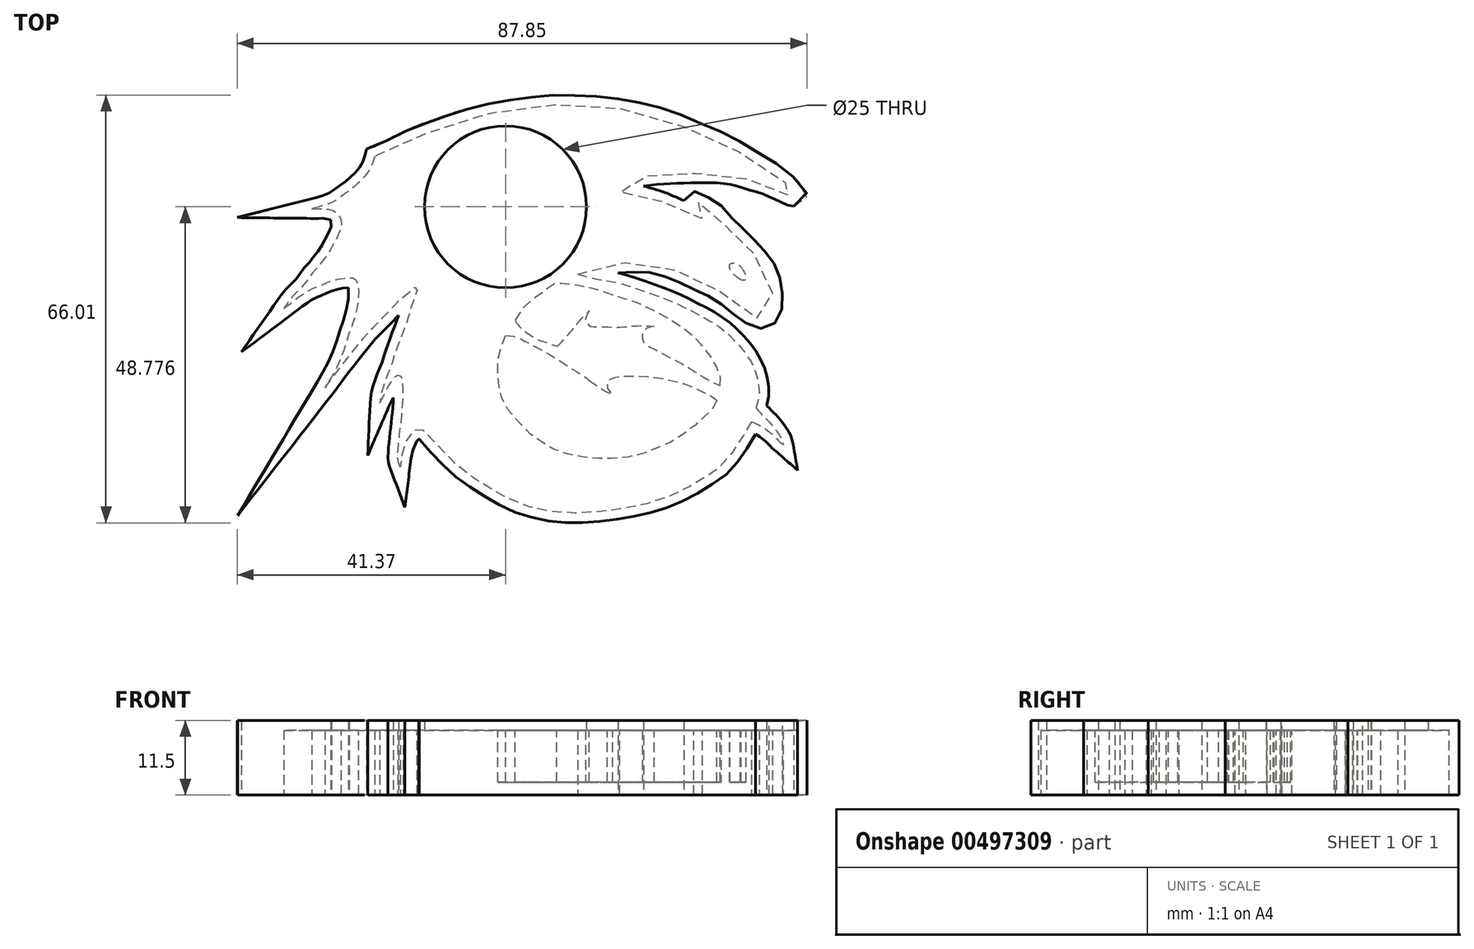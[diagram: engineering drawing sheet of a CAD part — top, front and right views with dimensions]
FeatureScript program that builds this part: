
annotation { "Feature Type Name" : "Feature", "Feature Type Description" : "" }
export const myFeature = defineFeature(function(context is Context, id is Id, definition is map)
    precondition{}
    {
        {
            var Q0;
            Q0=qCreatedBy(makeId("Top.planeOp"),FACE);
            var sketch = newSketch(context, id + "F0", { "sketchPlane" : qUnion([Q0])});
            skFitSpline(sketch, "E0", {"points": [v(3.09, 6.25) * mm, v(4.8, 5.75) * mm, v(7.76, 5.16) * mm, v(10.6, 4.54) * mm, v(13.82, 3.41) * mm, v(16.32, 2.53) * mm, v(19.29, 1.24) * mm, v(22.8, -0.6) * mm, v(25.68, -2.48) * mm, v(28.6, -5.48) * mm, v(30.18, -7.98) * mm, v(31.06, -11) * mm, v(30.99, -13.07) * mm, v(30.6, -14.4) * mm], "startDerivative": vector(25.97, -8.42) * mm, "endDerivative": vector(-8.12, -23.78) * mm});
            skFitSpline(sketch, "E1", {"points": [v(30.6, -14.4) * mm, v(31.45, -15.39) * mm, v(32.64, -16.58) * mm, v(33.62, -17.77) * mm, v(34.57, -19.25) * mm, v(34.82, -20.13) * mm], "startDerivative": vector(4.09, -5.06) * mm, "endDerivative": vector(0.92, -5.16) * mm});
            skFitSpline(sketch, "E2", {"points": [v(29.94, -16.55) * mm, v(30.85, -16.97) * mm, v(31.87, -17.53) * mm, v(32.92, -18.34) * mm, v(33.48, -18.86) * mm, v(34.12, -19.5) * mm, v(34.82, -20.13) * mm], "startDerivative": vector(5.46, -2.46) * mm, "endDerivative": vector(4.4, -3.84) * mm});
            skFitSpline(sketch, "E3", {"points": [v(29.94, -16.55) * mm, v(29.06, -18.02) * mm, v(27.3, -20.83) * mm, v(25.2, -23.43) * mm, v(23.33, -24.76) * mm, v(21.5, -25.92) * mm, v(18.98, -27.3) * mm, v(15.08, -28.84) * mm, v(11.5, -29.71) * mm, v(7.11, -30.38) * mm, v(2.02, -30.66) * mm, v(-2.2, -30.2) * mm, v(-5.85, -29.19) * mm, v(-9.43, -27.43) * mm, v(-11.67, -26.03) * mm, v(-14.98, -23.78) * mm, v(-16.73, -22.02) * mm, v(-17.85, -20.9) * mm, v(-19.19, -19.42) * mm, v(-20.6, -17.91) * mm, v(-21.12, -17.74) * mm, v(-21.82, -17.74) * mm, v(-22.6, -18.3) * mm, v(-23.26, -19.28) * mm, v(-23.82, -20.9) * mm, v(-24.1, -22.27) * mm, v(-24.28, -23.57) * mm], "startDerivative": vector(-24.88, -41.9) * mm, "endDerivative": vector(-5.74, -46.22) * mm});
            skFitSpline(sketch, "E4", {"points": [v(-24.28, -23.57) * mm, v(-24.6, -22.55) * mm, v(-24.6, -20.86) * mm, v(-24.08, -16.12) * mm, v(-23.88, -13.88) * mm, v(-23.8, -11.03) * mm, v(-23.93, -10) * mm, v(-24.02, -9.67) * mm, v(-24.49, -9.38) * mm, v(-24.95, -9.52) * mm, v(-25.48, -10.11) * mm, v(-26.07, -10.96) * mm, v(-26.6, -12.05) * mm, v(-27.12, -13.03) * mm, v(-27.4, -13.65) * mm], "startDerivative": vector(-5.7, 15.12) * mm, "endDerivative": vector(-4.81, -11.17) * mm});
            skFitSpline(sketch, "E5", {"points": [v(3.09, 6.25) * mm, v(4.64, 6.94) * mm, v(7.65, 7.65) * mm, v(10.1, 7.98) * mm, v(12.79, 8.07) * mm, v(15.27, 7.8) * mm, v(18.1, 6.88) * mm, v(20.5, 5.82) * mm, v(22.6, 4.82) * mm, v(25.07, 3.55) * mm, v(27.43, 1.75) * mm, v(28.64, 0.8) * mm, v(30.36, -0.32) * mm, v(31.42, -0.67) * mm, v(32.34, -0.4) * mm, v(32.9, 0.48) * mm, v(33.22, 1.8) * mm, v(33.1, 3.93) * mm, v(32.69, 5.85) * mm, v(31.83, 7.47) * mm, v(30.36, 9.3) * mm, v(28.97, 10.75) * mm, v(27.29, 12.38) * mm, v(26.34, 13.09) * mm, v(25.6, 14.09) * mm, v(24.6, 15.33) * mm, v(23.68, 16.04) * mm, v(22.5, 16.78) * mm, v(21.76, 17.22) * mm, v(21.23, 17.48) * mm, v(21.03, 17.43) * mm, v(21.08, 17.1) * mm, v(21.59, 16.54) * mm, v(22.18, 15.65) * mm, v(22.33, 14.89) * mm, v(22.06, 14.8) * mm, v(20.88, 15.42) * mm, v(18.75, 16.24) * mm, v(16.83, 17.1) * mm, v(14.74, 17.84) * mm, v(12.52, 18.43) * mm, v(10.43, 18.75) * mm, v(9.66, 18.93) * mm, v(9.66, 19.26) * mm, v(10.22, 20.14) * mm, v(10.72, 20.82) * mm, v(11.9, 21.12) * mm, v(14.94, 21.53) * mm, v(17.78, 21.7) * mm, v(20.08, 21.8) * mm, v(21.91, 21.8) * mm, v(24.8, 21.8) * mm, v(27.55, 21.38) * mm, v(29.68, 20.76) * mm, v(31.95, 20.08) * mm, v(34.7, 18.87) * mm, v(35.35, 18.58) * mm, v(36.09, 18.22) * mm, v(36.5, 18.22) * mm, v(36.85, 18.22) * mm, v(36.91, 18.64) * mm, v(36.09, 19.4) * mm, v(35.26, 20.2) * mm, v(32.6, 22.2) * mm, v(30.2, 23.66) * mm, v(27.2, 25.52) * mm, v(24.54, 26.85) * mm, v(20.64, 28.44) * mm, v(16.95, 30) * mm, v(12.4, 31.19) * mm, v(7.18, 32.07) * mm, v(2.6, 32.28) * mm, v(-1, 32.3) * mm, v(-6.2, 31.72) * mm, v(-10.07, 31.1) * mm, v(-14.88, 29.83) * mm, v(-18.4, 28.62) * mm, v(-22.5, 27.05) * mm, v(-25.6, 25.52) * mm, v(-28.23, 24.4) * mm], "startDerivative": vector(116.8, 60.87) * mm, "endDerivative": vector(-171.2, -68.47) * mm});
            skFitSpline(sketch, "E6", {"points": [v(-28.23, 24.4) * mm, v(-28.63, 23.07) * mm, v(-29.25, 21.96) * mm, v(-30.18, 20.79) * mm, v(-30.96, 20.06) * mm, v(-32.06, 19.15) * mm, v(-33, 18.48) * mm, v(-34.45, 17.49) * mm, v(-35.75, 16.93) * mm, v(-36.77, 16.62) * mm, v(-37.92, 16.32) * mm], "startDerivative": vector(-3.46, -13.35) * mm, "endDerivative": vector(-12.33, -3.13) * mm});
            skFitSpline(sketch, "E7", {"points": [v(-37.92, 16.32) * mm, v(-37.08, 16.32) * mm, v(-35.93, 16.32) * mm, v(-34.87, 16.12) * mm, v(-33.93, 15.61) * mm, v(-33.38, 14.44) * mm, v(-33.4, 13.43) * mm, v(-33.98, 11.97) * mm, v(-34.56, 10.86) * mm, v(-35.42, 9.34) * mm, v(-36.16, 8.35) * mm, v(-36.8, 7.5) * mm, v(-37.74, 6.43) * mm, v(-38.78, 5.04) * mm, v(-39.74, 3.92) * mm, v(-40.87, 2.76) * mm, v(-41.5, 1.97) * mm, v(-42.24, 0.93) * mm], "startDerivative": vector(16.65, -0.2) * mm, "endDerivative": vector(-12.9, -18.49) * mm});
            skFitSpline(sketch, "E8", {"points": [v(-42.24, 0.93) * mm, v(-41.28, 1.65) * mm, v(-40.12, 2.53) * mm, v(-39, 3.32) * mm, v(-38, 3.94) * mm, v(-36.9, 4.36) * mm, v(-35.5, 4.96) * mm, v(-34.64, 5.26) * mm, v(-33.37, 5.54) * mm, v(-32.45, 5.63) * mm, v(-31.68, 5.65) * mm, v(-31.46, 5.58) * mm, v(-31.26, 5.46) * mm, v(-31.11, 5.32) * mm, v(-30.95, 5.06) * mm, v(-30.83, 4.59) * mm, v(-30.67, 3.93) * mm, v(-30.7, 2.67) * mm, v(-30.82, 1.77) * mm, v(-31.02, 0.8) * mm, v(-31.38, -0.8) * mm, v(-31.68, -1.68) * mm, v(-32.18, -2.98) * mm, v(-32.46, -3.97) * mm, v(-32.82, -5.11) * mm, v(-33.37, -6.55) * mm, v(-33.8, -7.58) * mm, v(-34.64, -9.21) * mm, v(-35.87, -11.33) * mm], "startDerivative": vector(24.05, 17.91) * mm, "endDerivative": vector(-22.98, -38.6) * mm});
            skFitSpline(sketch, "E9", {"points": [v(-35.87, -11.33) * mm, v(-34.97, -10.16) * mm, v(-33.96, -8.77) * mm, v(-32.96, -7.45) * mm, v(-32.2, -6.5) * mm, v(-31.24, -5.27) * mm, v(-30.36, -4.17) * mm, v(-28.88, -2.43) * mm, v(-27.5, -1.08) * mm, v(-26.2, 0.3) * mm, v(-24.74, 1.83) * mm, v(-23.95, 2.61) * mm, v(-23.17, 3.17) * mm, v(-22.6, 3.66) * mm, v(-22.16, 4.08) * mm, v(-21.93, 4.25) * mm, v(-21.79, 4.23) * mm, v(-21.68, 4.16) * mm, v(-21.67, 3.75) * mm, v(-21.98, 2.75) * mm, v(-22.32, 1.8) * mm, v(-22.78, 0.46) * mm, v(-23.2, -0.96) * mm, v(-23.52, -1.93) * mm, v(-23.94, -2.95) * mm, v(-24.4, -4.23) * mm, v(-24.87, -5.43) * mm, v(-25.32, -6.7) * mm, v(-25.58, -7.62) * mm, v(-25.96, -8.7) * mm, v(-26.49, -9.94) * mm, v(-26.84, -11) * mm, v(-27.16, -12) * mm, v(-27.35, -12.92) * mm, v(-27.4, -13.65) * mm], "startDerivative": vector(26.23, 33.62) * mm, "endDerivative": vector(-1.36, -29.73) * mm});
            skSolve(sketch);
        }
        {
            var Q0;
            Q0=makeQuery(id+"F0.imprint","IMPRINT",FACE,{"disambiguationData":[TD([[makeQuery(id+"F0.imprint","IMPRINT",EDGE,{"derivedFrom":sQuery(id+"F0.wireOp",EDGE,"E0")}),-1.0]])]});
            extrude(context, id + "F1", {"entities" : qUnion([Q0]), "depth" : 10 * mm});
        }
        {
            var Q0;
            Q0=makeQuery(id+"F1.opExtrude","CAP_FACE",FACE,{"disambiguationData":[OSD([sQuery(id+"F0.wireOp",EDGE,"E0"),sQuery(id+"F0.wireOp",EDGE,"E1"),sQuery(id+"F0.wireOp",EDGE,"E2"),sQuery(id+"F0.wireOp",EDGE,"E3"),sQuery(id+"F0.wireOp",EDGE,"E4"),sQuery(id+"F0.wireOp",EDGE,"E5"),sQuery(id+"F0.wireOp",EDGE,"E6"),sQuery(id+"F0.wireOp",EDGE,"E7"),sQuery(id+"F0.wireOp",EDGE,"E8"),sQuery(id+"F0.wireOp",EDGE,"E9")])],"isStart":true});
            shell(context, id + "F2", {"entities" : qUnion([Q0]), "thickness" : 1.5 * mm, "oppositeDirection" : true});
        }
        {
            var Q0;
            Q0=makeQuery(id+"F2.opShell","OFFSET_FACE",FACE,{"disambiguationData":[OSD([sQuery(id+"F0.wireOp",EDGE,"E0"),sQuery(id+"F0.wireOp",EDGE,"E1"),sQuery(id+"F0.wireOp",EDGE,"E2"),sQuery(id+"F0.wireOp",EDGE,"E3"),sQuery(id+"F0.wireOp",EDGE,"E4"),sQuery(id+"F0.wireOp",EDGE,"E5"),sQuery(id+"F0.wireOp",EDGE,"E6"),sQuery(id+"F0.wireOp",EDGE,"E7"),sQuery(id+"F0.wireOp",EDGE,"E8"),sQuery(id+"F0.wireOp",EDGE,"E9")])]});
            var sketch = newSketch(context, id + "F3", { "sketchPlane" : qUnion([Q0])});
            skFitSpline(sketch, "E10", {"points": [v(-6.56, 0.95) * mm, v(-6.07, 1.61) * mm, v(-5.28, 2.41) * mm, v(-4.25, 3.16) * mm, v(-3.06, 3.86) * mm, v(-1.8, 4.3) * mm, v(-0.16, 4.92) * mm], "startDerivative": vector(3.32, 4.88) * mm, "endDerivative": vector(8.62, 3.44) * mm});
            skFitSpline(sketch, "E11", {"points": [v(-0.16, 4.92) * mm, v(0.34, 4.55) * mm, v(1.64, 3.1) * mm, v(2.57, 2.04) * mm, v(3.18, 1.25) * mm, v(3.86, 0.46) * mm, v(4.9, -0.56) * mm], "startDerivative": vector(3.71, -2.34) * mm, "endDerivative": vector(6, -5.72) * mm});
            skFitSpline(sketch, "E12", {"points": [v(4.9, -0.56) * mm, v(4.4, 0.38) * mm, v(4.33, 1.02) * mm, v(4.66, 1.48) * mm, v(5.15, 1.82) * mm, v(6.26, 1.89) * mm, v(7.63, 1.92) * mm, v(9.23, 1.98) * mm, v(10.99, 1.85) * mm, v(13.05, 1.73) * mm, v(14.9, 1.86) * mm], "startDerivative": vector(-6.25, 10.25) * mm, "endDerivative": vector(14.61, 1.57) * mm});
            skFitSpline(sketch, "E13", {"points": [v(14.9, 1.86) * mm, v(14, 2.05) * mm, v(13.36, 2.44) * mm, v(13.08, 3) * mm, v(13.13, 3.99) * mm, v(13.5, 4.56) * mm, v(14.74, 5.24) * mm, v(15.65, 5.72) * mm, v(16.52, 6.22) * mm, v(18.64, 7.3) * mm, v(20.47, 8.35) * mm, v(21.88, 9.28) * mm, v(22.97, 9.93) * mm, v(24.2, 10.63) * mm, v(25.05, 10.98) * mm], "startDerivative": vector(-14.88, 2.11) * mm, "endDerivative": vector(12.87, 4.55) * mm});
            skFitSpline(sketch, "E14", {"points": [v(25.05, 10.98) * mm, v(25.2, 10.46) * mm, v(24.99, 9.12) * mm, v(24.41, 7.8) * mm, v(23.12, 5.75) * mm, v(21.57, 4.02) * mm, v(20.54, 3.02) * mm, v(17.73, 1.03) * mm, v(16.34, 0.22) * mm, v(14.57, -0.69) * mm, v(13.15, -1.37) * mm, v(11.67, -2.02) * mm, v(9.7, -2.61) * mm, v(8.02, -3.18) * mm, v(6.1, -3.81) * mm, v(4.25, -4.27) * mm, v(1.55, -4.68) * mm, v(0.17, -4.74) * mm, v(-0.34, -4.7) * mm, v(-0.82, -4.6) * mm, v(-1.3, -4.22) * mm, v(-2.24, -3.37) * mm, v(-3.15, -2.82) * mm, v(-4.03, -2.15) * mm, v(-4.92, -1.38) * mm, v(-5.54, -0.66) * mm, v(-6.14, 0.23) * mm, v(-6.56, 0.95) * mm], "startDerivative": vector(8.43, -19.5) * mm, "endDerivative": vector(-13.9, 24.5) * mm});
            skFitSpline(sketch, "E15", {"points": [v(-8, 3.21) * mm, v(-6.28, 3.51) * mm, v(-4.74, 4.28) * mm, v(-3.31, 5.03) * mm, v(-1.8, 5.88) * mm, v(0.24, 7.08) * mm, v(1.94, 8.2) * mm, v(3.92, 9.43) * mm, v(4.85, 10.14) * mm], "startDerivative": vector(13.26, 1.26) * mm, "endDerivative": vector(12.73, 9.97) * mm});
            skFitSpline(sketch, "E16", {"points": [v(4.85, 10.14) * mm, v(5.7, 10.78) * mm, v(6.8, 11.46) * mm, v(7.86, 12.1) * mm, v(8.4, 12.4) * mm, v(8.48, 12.39) * mm, v(8.5, 12.3) * mm, v(8.37, 12.11) * mm, v(7.92, 11.69) * mm, v(7.68, 10.92) * mm, v(7.83, 10.27) * mm, v(8.29, 9.9) * mm, v(9.3, 9.6) * mm, v(10.71, 9.51) * mm, v(13.04, 9.55) * mm, v(16.1, 9.86) * mm, v(18.37, 10.4) * mm, v(20.56, 11.08) * mm, v(23.49, 12.52) * mm, v(23.77, 12.67) * mm, v(24.18, 12.94) * mm, v(24.6, 13.28) * mm], "startDerivative": vector(16.13, 12.6) * mm, "endDerivative": vector(27.28, 23.53) * mm});
            skFitSpline(sketch, "E17", {"points": [v(24.6, 13.28) * mm, v(24.32, 13.88) * mm, v(23.69, 14.8) * mm, v(22.96, 15.5) * mm, v(21.95, 16.5) * mm, v(20.85, 17.38) * mm, v(19, 18.75) * mm, v(17.54, 19.66) * mm, v(16.03, 20.34) * mm, v(14.03, 21.14) * mm, v(11.97, 21.85) * mm, v(9.62, 22.13) * mm, v(7.66, 22.26) * mm, v(5.97, 22.21) * mm, v(3.63, 21.97) * mm, v(1.81, 21.6) * mm, v(-0.1, 21.03) * mm, v(-1.56, 20.26) * mm, v(-3.1, 19.28) * mm, v(-4.5, 18.21) * mm, v(-6.12, 16.47) * mm, v(-7.68, 14.6) * mm, v(-8.43, 13.35) * mm, v(-8.87, 11.9) * mm, v(-9.1, 10.46) * mm, v(-9.2, 9) * mm, v(-9.21, 7.48) * mm, v(-8.96, 5.85) * mm, v(-8.39, 4.1) * mm, v(-8, 3.21) * mm], "startDerivative": vector(-10.8, 25.98) * mm, "endDerivative": vector(14.5, -30.3) * mm});
            skFitSpline(sketch, "E18", {"points": [v(28.34, -5.34) * mm, v(27.76, -5.7) * mm, v(27.05, -6.28) * mm, v(26.6, -6.95) * mm], "startDerivative": vector(-2.06, -1) * mm, "endDerivative": vector(-0.43, -1.96) * mm});
            skFitSpline(sketch, "E19", {"points": [v(26.6, -6.95) * mm, v(26.54, -7.21) * mm, v(26.57, -7.68) * mm, v(26.75, -7.87) * mm, v(27.2, -7.9) * mm, v(27.78, -7.76) * mm, v(28.2, -7.41) * mm], "startDerivative": vector(-0.36, -1.55) * mm, "endDerivative": vector(4.25, 3.77) * mm});
            skFitSpline(sketch, "E20", {"points": [v(28.2, -7.41) * mm, v(28.47, -7.06) * mm, v(28.87, -6.41) * mm, v(29.08, -5.86) * mm, v(29.06, -5.46) * mm, v(28.81, -5.28) * mm, v(28.34, -5.34) * mm], "startDerivative": vector(2.48, 2.7) * mm, "endDerivative": vector(-3.2, -1.87) * mm});
            skSolve(sketch);
        }
        {
            var Q0;
            Q0 = qSketchRegion(id + "F3", true);
            extrude(context, id + "F4", {"entities" : qUnion([Q0]), "operationType" : NewBodyOperationType.ADD, "depth" : 8 * mm, "offsetDistance" : 25 * mm});
        }
        {
            var Q0;
            Q0=makeQuery(id+"F2.opShell","OFFSET_FACE",FACE,{"disambiguationData":[OSD([sQuery(id+"F0.wireOp",EDGE,"E0"),sQuery(id+"F0.wireOp",EDGE,"E1"),sQuery(id+"F0.wireOp",EDGE,"E2"),sQuery(id+"F0.wireOp",EDGE,"E3"),sQuery(id+"F0.wireOp",EDGE,"E4"),sQuery(id+"F0.wireOp",EDGE,"E5"),sQuery(id+"F0.wireOp",EDGE,"E6"),sQuery(id+"F0.wireOp",EDGE,"E7"),sQuery(id+"F0.wireOp",EDGE,"E8"),sQuery(id+"F0.wireOp",EDGE,"E9")])]});
            var sketch = newSketch(context, id + "F5", { "sketchPlane" : qUnion([Q0])});
            skCircle(sketch, "E21", {"center": v(-8.03, -16.6) * mm, "radius": 12.5 * mm});
            skSolve(sketch);
        }
        {
            var Q0;
            Q0 = qSketchRegion(id + "F5", true);
            extrude(context, id + "F6", {"entities" : qUnion([Q0]), "operationType" : NewBodyOperationType.REMOVE, "oppositeDirection" : true, "depth" : 1.5 * mm});
        }
    });
